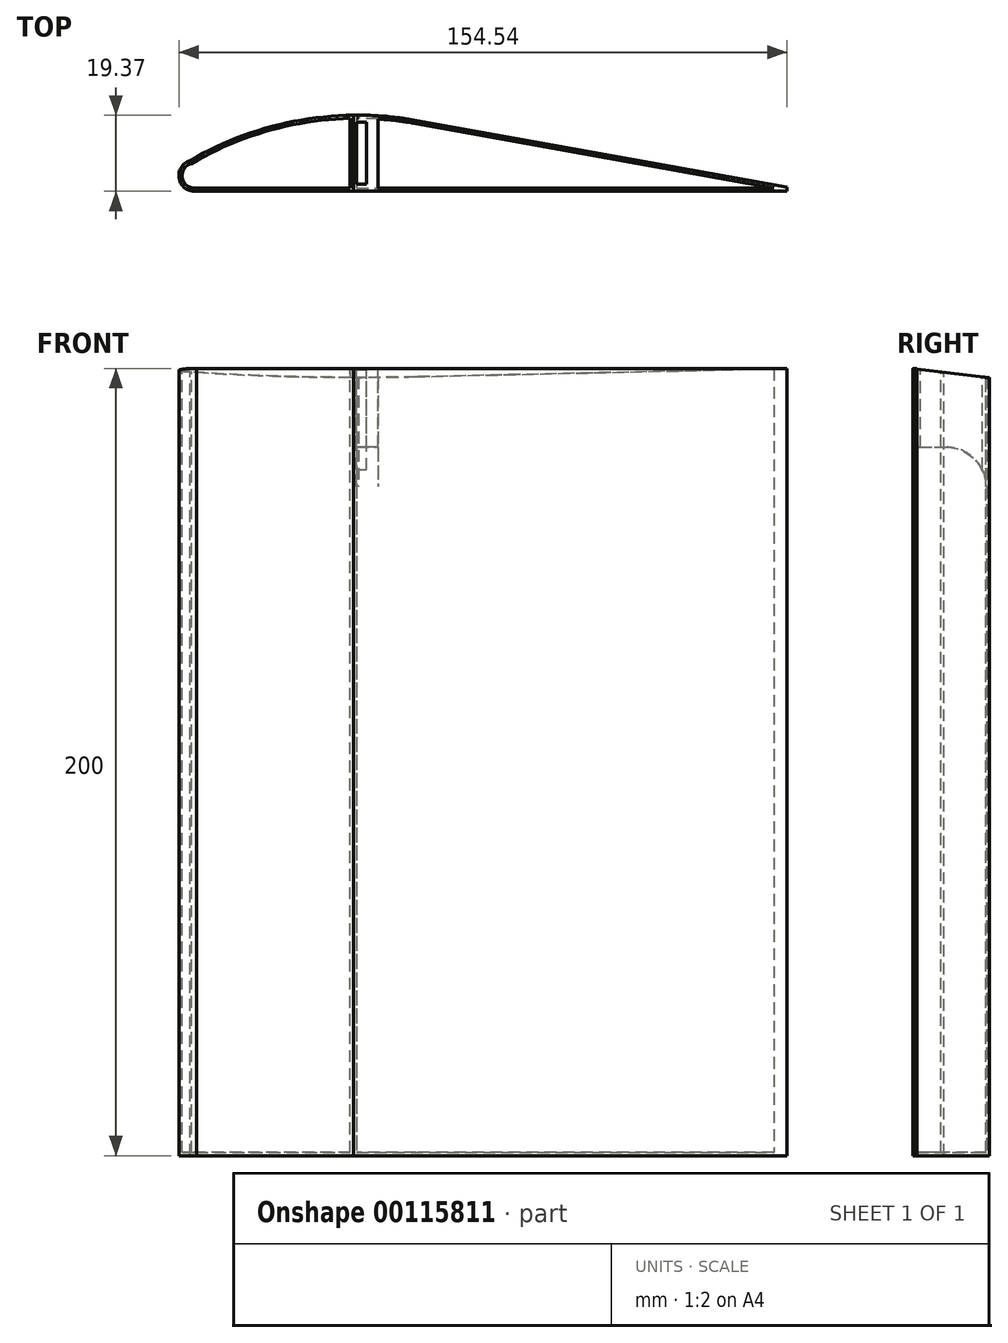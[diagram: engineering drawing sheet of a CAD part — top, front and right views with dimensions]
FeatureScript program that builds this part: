
annotation { "Feature Type Name" : "Feature", "Feature Type Description" : "" }
export const myFeature = defineFeature(function(context is Context, id is Id, definition is map)
    precondition{}
    {
        {
            var Q0;
            Q0=qCreatedBy(makeId("Top.planeOp"),FACE);
            var sketch = newSketch(context, id + "F0", { "sketchPlane" : qUnion([Q0])});
            skLineSegment(sketch, "E0", {"start": v(94.17, -2) * mm, "end": v(0, 15) * mm});
            skLineSegment(sketch, "E1", {"start": v(-55.86, -3) * mm, "end": v(94.14, -3) * mm});
            skLineSegment(sketch, "E2", {"start": v(94.14, -3) * mm, "end": v(94.17, -2) * mm});
            skArc(sketch, "E3", {"start": v(0, 15) * mm, "mid": v(-29.67, 15.05) * mm, "end": v(-57.5, 4.8) * mm});
            skArc(sketch, "E4", {"start": v(-57.5, 4.8) * mm, "mid": v(-60.28, 0.14) * mm, "end": v(-55.86, -3) * mm});
            skLineSegment(sketch, "E5", {"start": v(-16.04, 16.33) * mm, "end": v(-16.04, -3) * mm});
            skSolve(sketch);
        }
        {
            var Q0;
            {var subQ1=sQuery(id+"F0.wireOp",EDGE,"E0");Q0=makeQuery(id+"F0.imprint","IMPRINT",FACE,{"disambiguationData":[TD([[makeQuery(id+"F0.imprint","IMPRINT",EDGE,{"derivedFrom":subQ1}),1.0]])]});}
            extrude(context, id + "F1", {"entities" : qUnion([Q0]), "depth" : 200 * mm});
        }
        {
            var Q0;
            Q0=makeQuery(id+"F1.opExtrude","CAP_FACE",FACE,{"disambiguationData":[OSD([sQuery(id+"F0.wireOp",EDGE,"E0"),sQuery(id+"F0.wireOp",EDGE,"E1"),sQuery(id+"F0.wireOp",EDGE,"E2"),sQuery(id+"F0.wireOp",EDGE,"E3"),sQuery(id+"F0.wireOp",EDGE,"E4")])],"isStart":false});
            var sketch = newSketch(context, id + "F2", { "sketchPlane" : qUnion([Q0])});
            skLineSegment(sketch, "E6", {"start": v(94.17, -2) * mm, "end": v(0, 15) * mm});
            skLineSegment(sketch, "E7", {"start": v(-55.86, -3) * mm, "end": v(94.14, -3) * mm});
            skLineSegment(sketch, "E8", {"start": v(94.14, -3) * mm, "end": v(94.17, -2) * mm});
            skArc(sketch, "E9", {"start": v(0, 15) * mm, "mid": v(-29.67, 15.05) * mm, "end": v(-57.5, 4.8) * mm});
            skArc(sketch, "E10", {"start": v(-57.5, 4.8) * mm, "mid": v(-60.28, 0.14) * mm, "end": v(-55.86, -3) * mm});
            skLineSegment(sketch, "E11", {"start": v(-16.04, 16.33) * mm, "end": v(-16.04, -3) * mm});
            skSolve(sketch);
        }
        {
            var Q0;
            {var subQ2=sQuery(id+"F2.wireOp",EDGE,"E10");Q0=makeQuery(id+"F2.imprint","IMPRINT",FACE,{"disambiguationData":[TD([[makeQuery(id+"F2.imprint","IMPRINT",EDGE,{"derivedFrom":subQ2}),1.0]])]});}
            extrude(context, id + "F3", {"entities" : qUnion([Q0]), "oppositeDirection" : true, "depth" : 200 * mm});
        }
        {
            var Q0;
            Q0=makeQuery(id+"F1.opExtrude","CAP_FACE",FACE,{"disambiguationData":[OSD([sQuery(id+"F0.wireOp",EDGE,"E0"),sQuery(id+"F0.wireOp",EDGE,"E1"),sQuery(id+"F0.wireOp",EDGE,"E2"),sQuery(id+"F0.wireOp",EDGE,"E3"),sQuery(id+"F0.wireOp",EDGE,"E5")])],"isStart":false});
            var Q1;
            Q1=makeQuery(id+"F3.opExtrude","CAP_FACE",FACE,{"disambiguationData":[OSD([sQuery(id+"F2.wireOp",EDGE,"E7"),sQuery(id+"F2.wireOp",EDGE,"E9"),sQuery(id+"F2.wireOp",EDGE,"E10"),sQuery(id+"F2.wireOp",EDGE,"E11")])],"isStart":true});
            shell(context, id + "F4", {"entities" : qUnion([Q0, Q1]), "thickness" : .8 * mm});
        }
        {
            var Q0;
            Q0=makeQuery(id+"F1.opExtrude","CAP_FACE",FACE,{"disambiguationData":[OSD([sQuery(id+"F0.wireOp",EDGE,"E0"),sQuery(id+"F0.wireOp",EDGE,"E1"),sQuery(id+"F0.wireOp",EDGE,"E2"),sQuery(id+"F0.wireOp",EDGE,"E3"),sQuery(id+"F0.wireOp",EDGE,"E5")])],"isStart":false});
            var sketch = newSketch(context, id + "F5", { "sketchPlane" : qUnion([Q0])});
            skLineSegment(sketch, "E12.bottom", {"start": v(-12.74, -2.2) * mm, "end": v(-9.74, -2.2) * mm});
            skLineSegment(sketch, "E12.top", {"start": v(-12.74, 15.54) * mm, "end": v(-9.74, 15.54) * mm});
            skLineSegment(sketch, "E12.left", {"start": v(-12.74, -2.2) * mm, "end": v(-12.74, 15.54) * mm});
            skLineSegment(sketch, "E12.right", {"start": v(-9.74, -2.2) * mm, "end": v(-9.74, 15.54) * mm});
            skLineSegment(sketch, "E13.bottom", {"start": v(-12.74, 15.54) * mm, "end": v(-15.24, 15.54) * mm});
            skLineSegment(sketch, "E13.top", {"start": v(-12.74, 14.54) * mm, "end": v(-15.24, 14.54) * mm});
            skLineSegment(sketch, "E13.left", {"start": v(-12.74, 15.54) * mm, "end": v(-12.74, 14.54) * mm});
            skLineSegment(sketch, "E13.right", {"start": v(-15.24, 15.54) * mm, "end": v(-15.24, 14.54) * mm});
            skLineSegment(sketch, "E14.bottom", {"start": v(-12.74, -2.2) * mm, "end": v(-15.24, -2.2) * mm});
            skLineSegment(sketch, "E14.top", {"start": v(-12.74, -1.2) * mm, "end": v(-15.24, -1.2) * mm});
            skLineSegment(sketch, "E14.left", {"start": v(-12.74, -2.2) * mm, "end": v(-12.74, -1.2) * mm});
            skLineSegment(sketch, "E14.right", {"start": v(-15.24, -2.2) * mm, "end": v(-15.24, -1.2) * mm});
            skSolve(sketch);
        }
        {
            var Q0;
            Q0=qSketchRegion(id+"F5",true);
            extrude(context, id + "F6", {"entities" : qUnion([Q0]), "operationType" : NewBodyOperationType.ADD, "oppositeDirection" : true, "depth" : 20 * mm});
        }
        {
            var Q0;
            {var subQ0=sQuery(id+"F0.wireOp",EDGE,"E3");Q0=makeQuery(id+"F6.boolean.opBoolean","INTERSECT",EDGE,{"derivedFrom":[makeQuery(id+"FlvnLV0fvoY6EBe_2.boolean.opBoolean","MERGE",FACE,{"derivedFrom":[makeQuery(id+"F4.opShell","OFFSET_FACE",FACE,{"disambiguationData":[OSD([subQ0])]}),makeQuery(id+"FlvnLV0fvoY6EBe_2.opExtrude","SWEPT_FACE",FACE,{"disambiguationData":[OSD([subQ0])]})]}),makeQuery(id+"F6.opExtrude","CAP_FACE",FACE,{"disambiguationData":[OSD([sQuery(id+"F5.wireOp",EDGE,"E12.bottom"),sQuery(id+"F5.wireOp",EDGE,"E12.top"),sQuery(id+"F5.wireOp",EDGE,"E12.left"),sQuery(id+"F5.wireOp",EDGE,"E12.right")])],"isStart":false})]});}
            var Q1;
            Q1=makeQuery(id+"F6.opExtrude","CAP_EDGE",EDGE,{"disambiguationData":[OSD([sQuery(id+"F5.wireOp",EDGE,"E12.bottom")])],"isStart":false});
            fillet(context, id + "F7", {"entities" : qUnion([Q0, Q1]), "radius" : 10 * mm, "tangentPropagation" : true, "allowEdgeOverflow" : false});
        }
        {
            var Q0;
            Q0=makeQuery(id+"F6.boolean.opBoolean","MERGE",FACE,{"derivedFrom":[makeQuery(id+"F1.opExtrude","CAP_FACE",FACE,{"disambiguationData":[OSD([sQuery(id+"F0.wireOp",EDGE,"E0"),sQuery(id+"F0.wireOp",EDGE,"E1"),sQuery(id+"F0.wireOp",EDGE,"E2"),sQuery(id+"F0.wireOp",EDGE,"E3"),sQuery(id+"F0.wireOp",EDGE,"E5")])],"isStart":false}),makeQuery(id+"F6.opExtrude","CAP_FACE",FACE,{"disambiguationData":[OSD([sQuery(id+"F5.wireOp",EDGE,"E12.bottom"),sQuery(id+"F5.wireOp",EDGE,"E12.top"),sQuery(id+"F5.wireOp",EDGE,"E12.left"),sQuery(id+"F5.wireOp",EDGE,"E12.right"),sQuery(id+"F5.wireOp",EDGE,"E13.bottom"),sQuery(id+"F5.wireOp",EDGE,"E13.top"),sQuery(id+"F5.wireOp",EDGE,"E13.right"),sQuery(id+"F5.wireOp",EDGE,"E14.bottom"),sQuery(id+"F5.wireOp",EDGE,"E14.top"),sQuery(id+"F5.wireOp",EDGE,"E14.right")])],"isStart":true})]});
            var sketch = newSketch(context, id + "F8", { "sketchPlane" : qUnion([Q0])});
            skLineSegment(sketch, "E15.bottom", {"start": v(94.14, -3) * mm, "end": v(-61.05, -3) * mm});
            skLineSegment(sketch, "E15.top", {"start": v(94.14, 19.34) * mm, "end": v(-61.05, 19.34) * mm});
            skLineSegment(sketch, "E15.left", {"start": v(94.14, -3) * mm, "end": v(94.14, 19.34) * mm});
            skLineSegment(sketch, "E15.right", {"start": v(-61.05, -3) * mm, "end": v(-61.05, 19.34) * mm});
            skSolve(sketch);
        }
        {
            var Q0;
            Q0 = qSketchRegion(id + "F8", true);
            var Q1;
            Q1=sQuery(id+"F8.wireOp",EDGE,"E15.bottom");
            revolve(context, id + "F9", {"operationType" : NewBodyOperationType.REMOVE, "entities" : qUnion([Q0]), "axis" : qUnion([Q1]), "revolveType" : RevolveType.ONE_DIRECTION, "angle" : 7 * degree});
        }
    });
